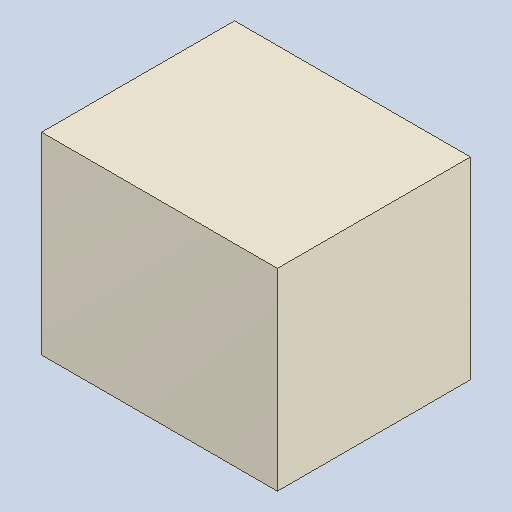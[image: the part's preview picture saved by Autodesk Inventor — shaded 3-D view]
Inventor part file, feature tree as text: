
AUTODESK INVENTOR PART (.ipt)
format: ipt  version: 2023.4 (Build 274418000, 418)  size: 81,920 bytes
history: native  units: mm
features: extrude x1
ambient origin geometry x8: Origin, YZ Plane, XZ Plane, XY Plane, X Axis, Y Axis, Z Axis, Center Point
bodies: Solid1 (feature_tree)
feature tree (1):
  extrude  "Extruded_15"  [1 undecoded]
note: 1 required parameter value undecoded (feature->parameter linkage not recoverable at this tier; creation-order binding heuristic only, values carry confidence <= 0.55)
